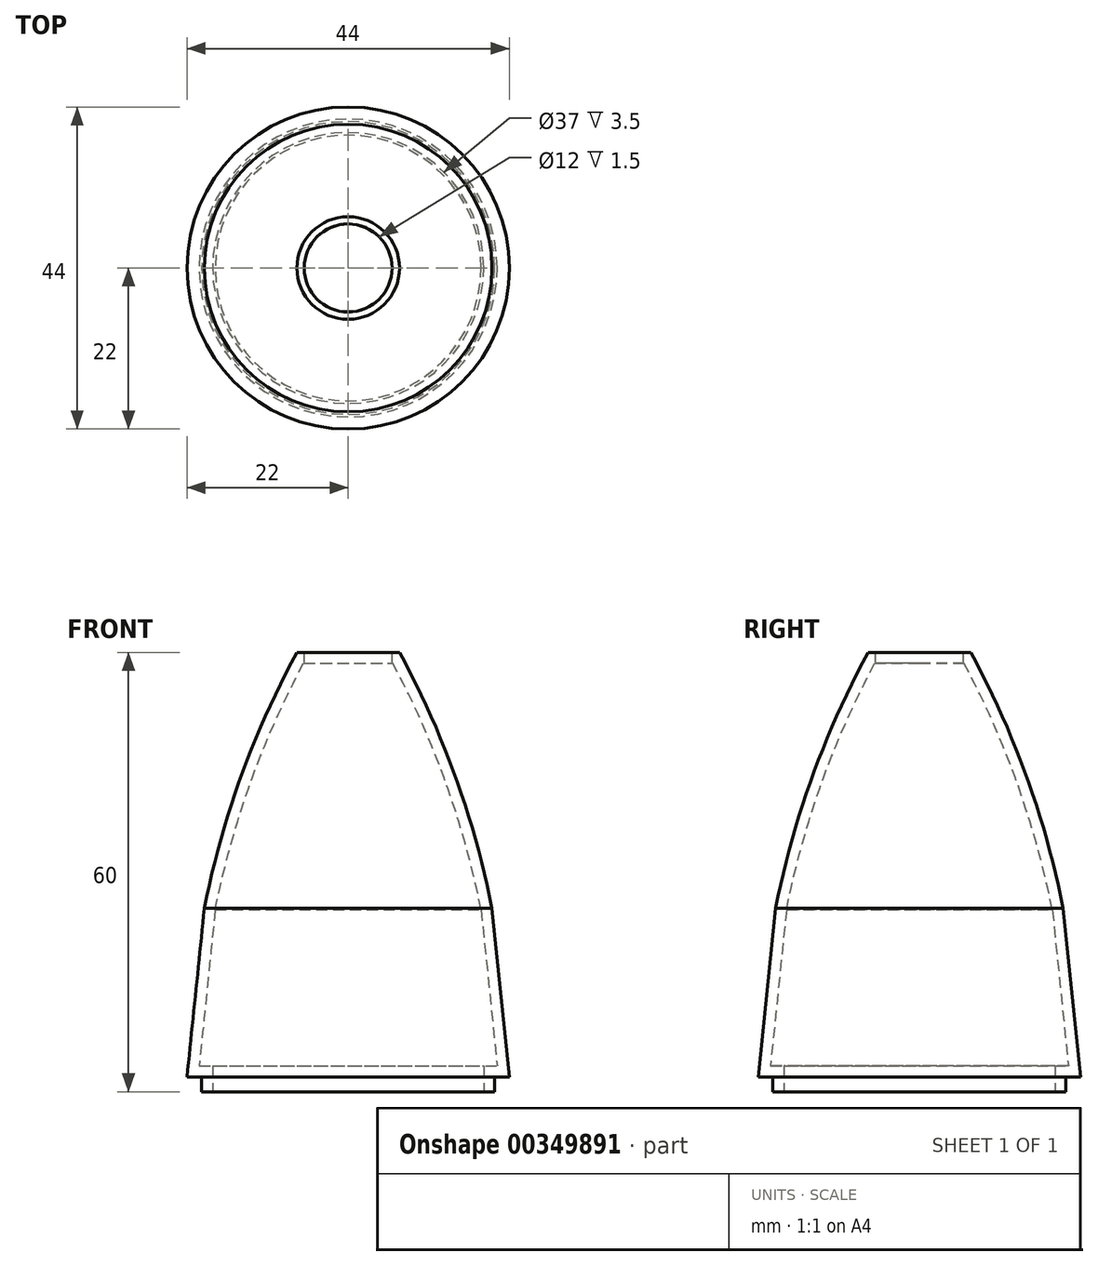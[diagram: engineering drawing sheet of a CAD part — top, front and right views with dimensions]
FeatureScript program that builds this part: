
annotation { "Feature Type Name" : "Feature", "Feature Type Description" : "" }
export const myFeature = defineFeature(function(context is Context, id is Id, definition is map)
    precondition{}
    {
        {
            var Q0;
            Q0=qCreatedBy(makeId("Front.planeOp"),FACE);
            var sketch = newSketch(context, id + "F0", { "sketchPlane" : qUnion([Q0])});
            skLineSegment(sketch, "E0", {"start": v(-20, 0) * mm, "end": v(-20, 2) * mm});
            skLineSegment(sketch, "E1", {"start": v(-20, 2) * mm, "end": v(-22, 2) * mm});
            skLineSegment(sketch, "E2", {"start": v(-22, 2) * mm, "end": v(-19.63, 25.06) * mm});
            skLineSegment(sketch, "E3", {"start": v(0, 60) * mm, "end": v(-7, 60) * mm});
            skLineSegment(sketch, "E4", {"start": v(0, 0) * mm, "end": v(0, 60) * mm});
            skLineSegment(sketch, "E5", {"start": v(0, 0) * mm, "end": v(-20, 0) * mm});
            skArc(sketch, "E6", {"start": v(-7, 60) * mm, "mid": v(-14.64, 43) * mm, "end": v(-19.63, 25.06) * mm});
            skSolve(sketch);
        }
        {
            var Q0;
            Q0=makeQuery(id+"F0.imprint","IMPRINT",FACE,{"disambiguationData":[TD([[makeQuery(id+"F0.imprint","IMPRINT",EDGE,{"derivedFrom":sQuery(id+"F0.wireOp",EDGE,"E0")}),-1.0]])]});
            var Q1;
            Q1=sQuery(id+"F0.wireOp",EDGE,"E4");
            revolve(context, id + "F1", {"entities" : qUnion([Q0]), "axis" : qUnion([Q1]), "revolveType" : RevolveType.FULL});
        }
        {
            var Q0;
            Q0=makeQuery(id+"F1.opRevolve","SWEPT_FACE",FACE,{"disambiguationData":[OSD([sQuery(id+"F0.wireOp",EDGE,"E5")])]});
            shell(context, id + "F2", {"entities" : qUnion([Q0]), "thickness" : 1.5 * mm});
        }
        {
            var Q0;
            Q0=makeQuery(id+"F1.opRevolve","SWEPT_FACE",FACE,{"disambiguationData":[OSD([sQuery(id+"F0.wireOp",EDGE,"E3")])]});
            var sketch = newSketch(context, id + "F3", { "sketchPlane" : qUnion([Q0])});
            skPoint(sketch, "E7", {"position": v(0, 0) * mm});
            skSolve(sketch);
        }
        {
            var Q0;
            Q0=sQuery(id+"F3.wireOp",VERTEX,"E7");
            var Q1;
            Q1=makeQuery(id+"F1.opRevolve","SWEPT_BODY",BODY,{"disambiguationData":[OSD([sQuery(id+"F0.wireOp",EDGE,"E0"),sQuery(id+"F0.wireOp",EDGE,"E1"),sQuery(id+"F0.wireOp",EDGE,"E2"),sQuery(id+"F0.wireOp",EDGE,"E3"),sQuery(id+"F0.wireOp",EDGE,"E4"),sQuery(id+"F0.wireOp",EDGE,"E5"),sQuery(id+"F0.wireOp",EDGE,"E6")])]});
            hole(context, id + "F4", {"style" : HoleStyle.SIMPLE, "endStyle" : HoleEndStyle.THROUGH, "holeDiameter" : 12 * mm, "isTappedThrough" : true, "tappedDepth" : 12 * mm, "tapClearance" : 3, "locations" : qUnion([Q0]), "scope" : qUnion([Q1])});
        }
    });
